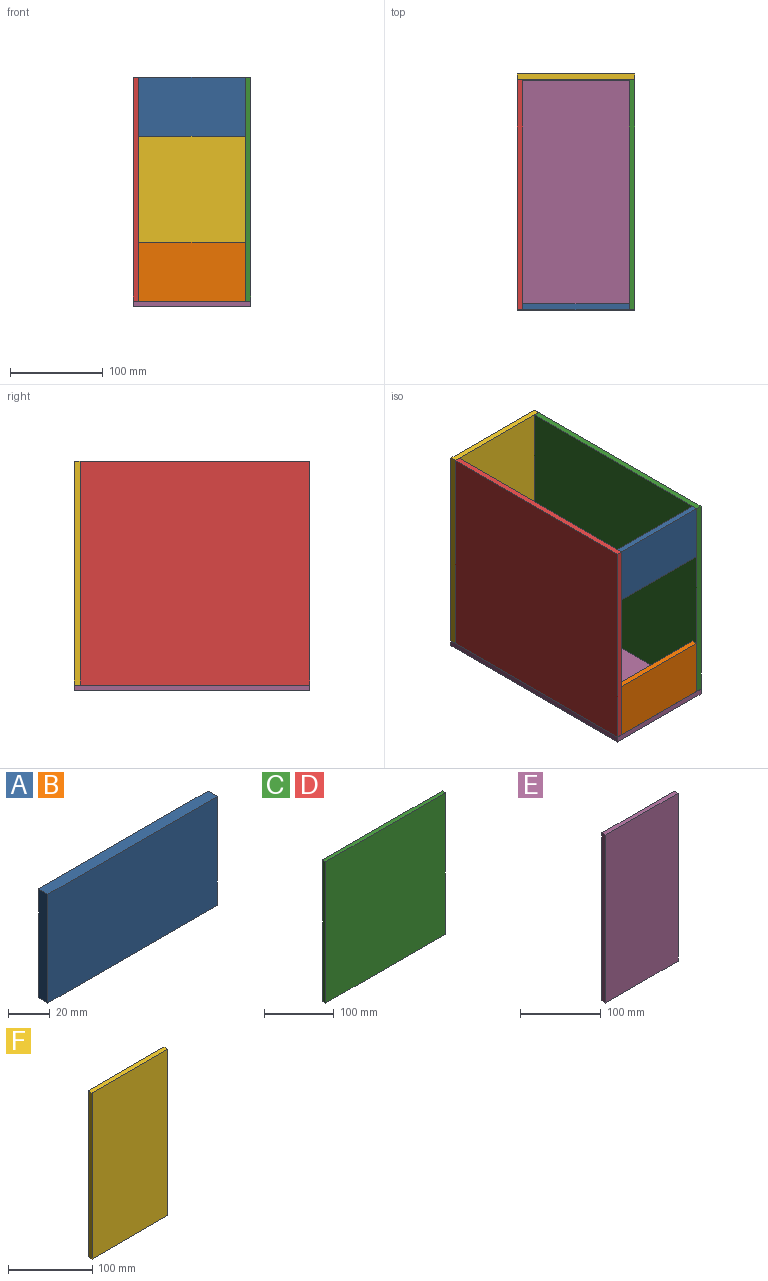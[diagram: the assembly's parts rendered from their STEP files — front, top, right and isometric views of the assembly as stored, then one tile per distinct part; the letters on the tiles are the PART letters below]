
ASSEMBLY  parts=6 mates=5
PART A: 6 faces, bbox 114.3x6.4x63.5 mm
  f0: plane 63.5x6.35mm, normal (-1,0,0), area 403.2mm2, adj f1,f3,f4,f5
  f1: plane 114.3x6.35mm, normal (0,0,-1), area 725.8mm2, adj f0,f2,f4,f5
  f2: plane 63.5x6.35mm, normal (1,0,0), area 403.2mm2, adj f1,f3,f4,f5
  f3: plane 114.3x6.35mm, normal (0,0,1), area 725.8mm2, adj f0,f2,f4,f5
  f4: plane 114.3x63.5mm, normal (0,-1,0), area 7258.1mm2, adj f0,f1,f2,f3
  f5: plane 114.3x63.5mm, normal (0,1,0), area 7258.1mm2, adj f0,f1,f2,f3
PART B: same geometry as A
PART C: 6 faces, bbox 241.3x6.4x247.7 mm
  f0: plane 241.3x6.35mm, normal (0,0,1), area 1532.3mm2, adj f1,f3,f4,f5
  f1: plane 247.65x6.35mm, normal (-1,0,0), area 1572.6mm2, adj f0,f2,f4,f5
  f2: plane 241.3x6.35mm, normal (0,0,-1), area 1532.3mm2, adj f1,f3,f4,f5
  f3: plane 247.65x6.35mm, normal (1,0,0), area 1572.6mm2, adj f0,f2,f4,f5
  f4: plane 247.65x241.3mm, normal (0,-1,0), area 59757.9mm2, adj f0,f1,f2,f3
  f5: plane 247.65x241.3mm, normal (0,1,0), area 59757.9mm2, adj f0,f1,f2,f3
PART D: same geometry as C
PART E: 6 faces, bbox 127x6.4x254 mm
  f0: plane 127x6.35mm, normal (0,0,1), area 806.5mm2, adj f1,f3,f4,f5
  f1: plane 254x6.35mm, normal (-1,0,0), area 1612.9mm2, adj f0,f2,f4,f5
  f2: plane 127x6.35mm, normal (0,0,-1), area 806.5mm2, adj f1,f3,f4,f5
  f3: plane 254x6.35mm, normal (1,0,0), area 1612.9mm2, adj f0,f2,f4,f5
  f4: plane 254x127mm, normal (0,-1,0), area 32258mm2, adj f0,f1,f2,f3
  f5: plane 254x127mm, normal (0,1,0), area 32258mm2, adj f0,f1,f2,f3
PART F: 6 faces, bbox 127x6.4x241.3 mm
  f0: plane 127x6.35mm, normal (0,0,1), area 806.5mm2, adj f1,f3,f4,f5
  f1: plane 241.3x6.35mm, normal (-1,0,0), area 1532.3mm2, adj f0,f2,f4,f5
  f2: plane 127x6.35mm, normal (0,0,-1), area 806.5mm2, adj f1,f3,f4,f5
  f3: plane 241.3x6.35mm, normal (1,0,0), area 1532.3mm2, adj f0,f2,f4,f5
  f4: plane 241.3x127mm, normal (0,-1,0), area 30645.1mm2, adj f0,f1,f2,f3
  f5: plane 241.3x127mm, normal (0,1,0), area 30645.1mm2, adj f0,f1,f2,f3
PLACE A rot(axis=(1,0,0),0deg) t=(-280.21,41,240.91)mm
PLACE B rot(axis=(1,0,0),0deg) t=(-280.21,41,63.11)mm
PLACE C rot(axis=(-0.58,-0.58,-0.58),120deg) t=(223.63,103.26,235.8)mm
PLACE D rot(axis=(-0.58,-0.58,-0.58),120deg) t=(102.98,103.26,235.8)mm
PLACE E rot(axis=(1,0,0),90deg) t=(-44.39,220.03,-5.5)mm
PLACE F rot(axis=(1,0,0),0deg) t=(577.12,288.65,63.11)mm
MATE fastened B.f1 <-> E.f5  axis (0,0,-1) through (160.13,34.65,-5.5)mm
MATE fastened A.f2 <-> C.f4  axis (1,0,0) through (217.28,34.65,235.8)mm
MATE fastened F.f4 <-> C.f0  axis (0,-1,0) through (223.63,282.3,115.15)mm
MATE fastened D.f0 <-> F.f4  axis (0,1,0) through (96.63,282.3,115.15)mm
MATE fastened E.f5 <-> F.f2  axis (0,0,1) through (160.13,288.65,-5.5)mm
